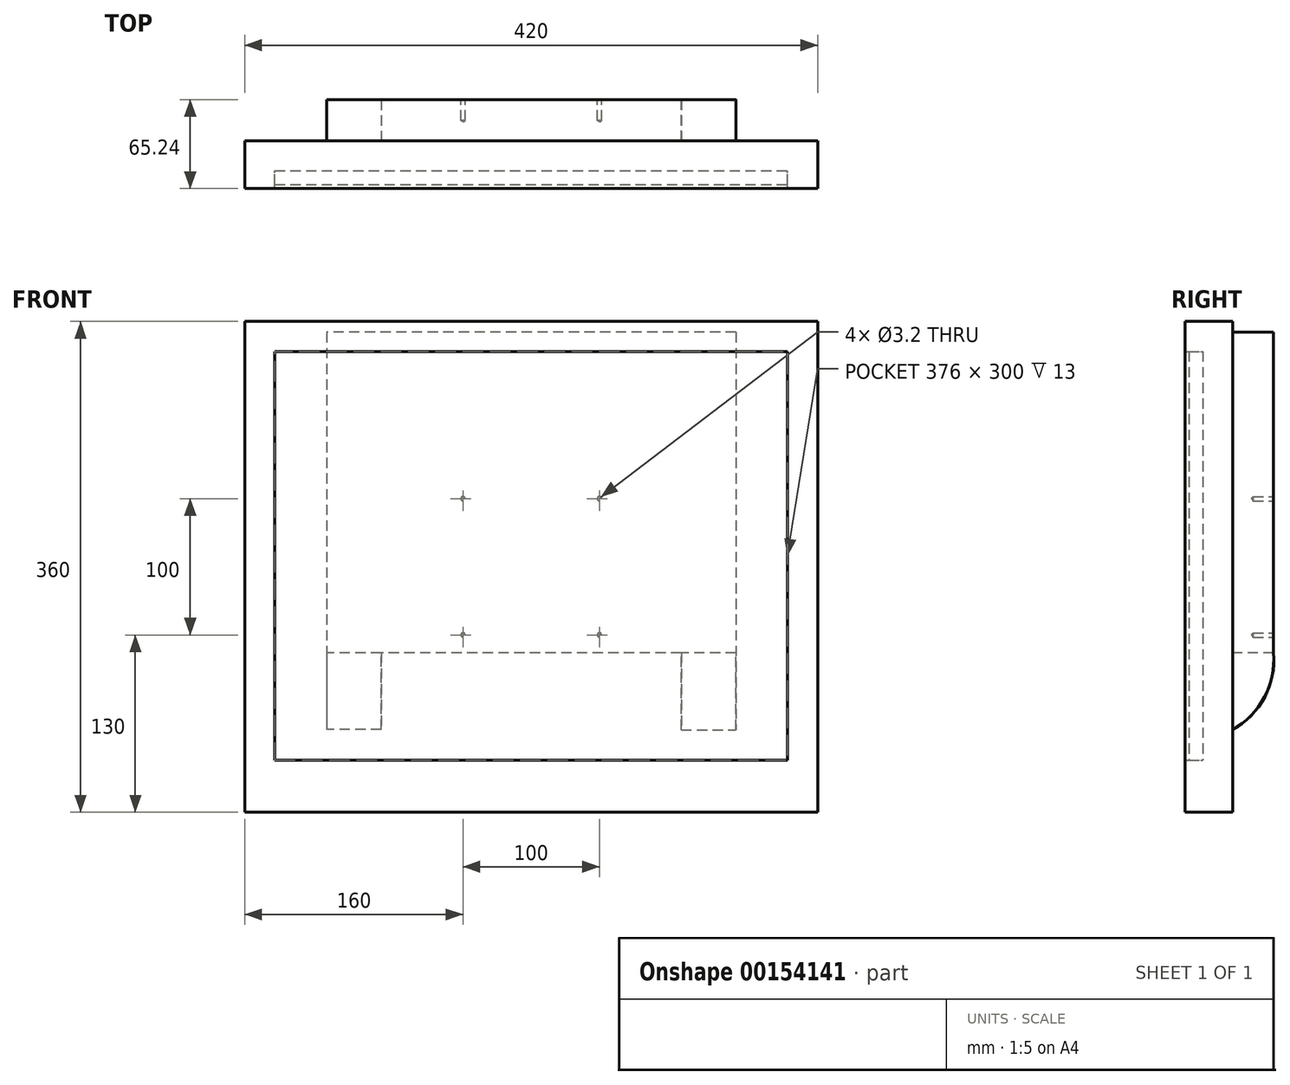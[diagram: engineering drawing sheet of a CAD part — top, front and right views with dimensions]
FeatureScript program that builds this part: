
annotation { "Feature Type Name" : "Feature", "Feature Type Description" : "" }
export const myFeature = defineFeature(function(context is Context, id is Id, definition is map)
    precondition{}
    {
        {
            var Q0;
            Q0=qCreatedBy(makeId("Front.planeOp"),FACE);
            var sketch = newSketch(context, id + "F0", { "sketchPlane" : qUnion([Q0])});
            skLineSegment(sketch, "E0.bottom", {"start": v(210, -180) * mm, "end": v(-210, -180) * mm});
            skLineSegment(sketch, "E0.top", {"start": v(210, 180) * mm, "end": v(-210, 180) * mm});
            skLineSegment(sketch, "E0.left", {"start": v(210, -180) * mm, "end": v(210, 180) * mm});
            skLineSegment(sketch, "E0.right", {"start": v(-210, -180) * mm, "end": v(-210, 180) * mm});
            skPoint(sketch, "E0.middle", {"position": v(0, 0) * mm});
            skLineSegment(sketch, "E1.bottom", {"start": v(-188, 158) * mm, "end": v(188, 158) * mm});
            skLineSegment(sketch, "E1.top", {"start": v(-188, -142) * mm, "end": v(188, -142) * mm});
            skLineSegment(sketch, "E1.left", {"start": v(-188, 158) * mm, "end": v(-188, -142) * mm});
            skLineSegment(sketch, "E1.right", {"start": v(188, 158) * mm, "end": v(188, -142) * mm});
            skSolve(sketch);
        }
        {
            var Q0;
            Q0 = qSketchRegion(id + "F0", true);
            extrude(context, id + "F1", {"entities" : qUnion([Q0]), "depth" : 13 * mm});
        }
        {
            var Q0;
            Q0=makeQuery(id+"F1.opExtrude","CAP_FACE",FACE,{"disambiguationData":[OSD([sQuery(id+"F0.wireOp",EDGE,"E0.bottom"),sQuery(id+"F0.wireOp",EDGE,"E0.top"),sQuery(id+"F0.wireOp",EDGE,"E0.left"),sQuery(id+"F0.wireOp",EDGE,"E0.right"),sQuery(id+"F0.wireOp",EDGE,"E1.bottom"),sQuery(id+"F0.wireOp",EDGE,"E1.top"),sQuery(id+"F0.wireOp",EDGE,"E1.left"),sQuery(id+"F0.wireOp",EDGE,"E1.right")])],"isStart":true});
            var sketch = newSketch(context, id + "F2", { "sketchPlane" : qUnion([Q0])});
            skLineSegment(sketch, "E2.bottom", {"start": v(-210, 180) * mm, "end": v(210, 180) * mm});
            skLineSegment(sketch, "E2.top", {"start": v(-210, -180) * mm, "end": v(210, -180) * mm});
            skLineSegment(sketch, "E2.left", {"start": v(-210, 180) * mm, "end": v(-210, -180) * mm});
            skLineSegment(sketch, "E2.right", {"start": v(210, 180) * mm, "end": v(210, -180) * mm});
            skSolve(sketch);
        }
        {
            var Q0;
            Q0 = qSketchRegion(id + "F2", true);
            extrude(context, id + "F3", {"entities" : qUnion([Q0]), "operationType" : NewBodyOperationType.ADD, "depth" : 22 * mm});
        }
        {
            var Q0;
            Q0=makeQuery(id+"F3.opExtrude","CAP_FACE",FACE,{"disambiguationData":[OSD([sQuery(id+"F2.wireOp",EDGE,"E2.bottom"),sQuery(id+"F2.wireOp",EDGE,"E2.top"),sQuery(id+"F2.wireOp",EDGE,"E2.left"),sQuery(id+"F2.wireOp",EDGE,"E2.right")])],"isStart":true});
            var sketch = newSketch(context, id + "F4", { "sketchPlane" : qUnion([Q0])});
            skLineSegment(sketch, "E3.bottom", {"start": v(-188, 158) * mm, "end": v(188, 158) * mm});
            skLineSegment(sketch, "E3.top", {"start": v(-188, -142) * mm, "end": v(188, -142) * mm});
            skLineSegment(sketch, "E3.left", {"start": v(-188, 158) * mm, "end": v(-188, -142) * mm});
            skLineSegment(sketch, "E3.right", {"start": v(188, 158) * mm, "end": v(188, -142) * mm});
            skSolve(sketch);
        }
        {
            var Q0;
            Q0 = qSketchRegion(id + "F4", true);
            extrude(context, id + "F5", {"entities" : qUnion([Q0]), "depth" : 10 * mm});
        }
        {
            var Q0;
            Q0=makeQuery(id+"F3.opExtrude","CAP_FACE",FACE,{"disambiguationData":[OSD([sQuery(id+"F2.wireOp",EDGE,"E2.bottom"),sQuery(id+"F2.wireOp",EDGE,"E2.top"),sQuery(id+"F2.wireOp",EDGE,"E2.left"),sQuery(id+"F2.wireOp",EDGE,"E2.right")])],"isStart":false});
            var sketch = newSketch(context, id + "F6", { "sketchPlane" : qUnion([Q0])});
            skLineSegment(sketch, "E4.bottom", {"start": v(-150, 172) * mm, "end": v(150, 172) * mm});
            skLineSegment(sketch, "E4.top", {"start": v(-150, -63) * mm, "end": v(150, -63) * mm});
            skLineSegment(sketch, "E4.left", {"start": v(-150, 172) * mm, "end": v(-150, -63) * mm});
            skLineSegment(sketch, "E4.right", {"start": v(150, 172) * mm, "end": v(150, -63) * mm});
            skSolve(sketch);
        }
        {
            var Q0;
            Q0 = qSketchRegion(id + "F6", true);
            extrude(context, id + "F7", {"entities" : qUnion([Q0]), "operationType" : NewBodyOperationType.ADD, "depth" : 30 * mm});
        }
        {
            var Q0;
            Q0=makeQuery(id+"F7.opExtrude","SWEPT_FACE",FACE,{"disambiguationData":[OSD([sQuery(id+"F6.wireOp",EDGE,"E4.left")])]});
            var sketch = newSketch(context, id + "F8", { "sketchPlane" : qUnion([Q0])});
            skArc(sketch, "E5", {"start": v(21.9, -119.54) * mm, "mid": v(45.19, -95.66) * mm, "end": v(52, -63) * mm});
            skLineSegment(sketch, "E6", {"start": v(52, -63) * mm, "end": v(22, -63) * mm});
            skLineSegment(sketch, "E7", {"start": v(22, -63) * mm, "end": v(21.9, -119.54) * mm});
            skSolve(sketch);
        }
        {
            var Q0;
            Q0 = qSketchRegion(id + "F8", true);
            extrude(context, id + "F9", {"entities" : qUnion([Q0]), "operationType" : NewBodyOperationType.ADD, "oppositeDirection" : true, "depth" : 40 * mm});
        }
        {
            var Q0;
            Q0=makeQuery(id+"F7.opExtrude","SWEPT_FACE",FACE,{"disambiguationData":[OSD([sQuery(id+"F6.wireOp",EDGE,"E4.right")])]});
            var sketch = newSketch(context, id + "F10", { "sketchPlane" : qUnion([Q0])});
            skArc(sketch, "E8", {"start": v(-52, -63) * mm, "mid": v(-45.4, -95.72) * mm, "end": v(-21.9, -119.45) * mm});
            skLineSegment(sketch, "E9", {"start": v(-52, -63) * mm, "end": v(-22, -63) * mm});
            skLineSegment(sketch, "E10", {"start": v(-22, -63) * mm, "end": v(-21.9, -119.45) * mm});
            skSolve(sketch);
        }
        {
            var Q0;
            Q0 = qSketchRegion(id + "F10", true);
            extrude(context, id + "F11", {"entities" : qUnion([Q0]), "operationType" : NewBodyOperationType.ADD, "oppositeDirection" : true, "depth" : 40 * mm});
        }
        {
            var Q0;
            Q0=makeQuery(id+"F7.opExtrude","CAP_FACE",FACE,{"disambiguationData":[OSD([sQuery(id+"F6.wireOp",EDGE,"E4.bottom"),sQuery(id+"F6.wireOp",EDGE,"E4.top"),sQuery(id+"F6.wireOp",EDGE,"E4.left"),sQuery(id+"F6.wireOp",EDGE,"E4.right")])],"isStart":false});
            var sketch = newSketch(context, id + "F12", { "sketchPlane" : qUnion([Q0])});
            skPoint(sketch, "E11", {"position": v(50, -50) * mm});
            skPoint(sketch, "E12", {"position": v(50, 50) * mm});
            skPoint(sketch, "E13", {"position": v(-50, 50) * mm});
            skPoint(sketch, "E14", {"position": v(-50, -50) * mm});
            skLineSegment(sketch, "E15", {"start": v(-50, 50) * mm, "end": v(50, 50) * mm});
            skLineSegment(sketch, "E16", {"start": v(50, 50) * mm, "end": v(50, -50) * mm});
            skLineSegment(sketch, "E17", {"start": v(50, -50) * mm, "end": v(-50, -50) * mm});
            skLineSegment(sketch, "E18", {"start": v(-50, -50) * mm, "end": v(-50, 50) * mm});
            skSolve(sketch);
        }
        {
            var Q0;
            Q0=sQuery(id+"F12.wireOp",VERTEX,"E13");
            var Q1;
            Q1=sQuery(id+"F12.wireOp",VERTEX,"E12");
            var Q2;
            Q2=sQuery(id+"F12.wireOp",VERTEX,"E11");
            var Q3;
            Q3=sQuery(id+"F12.wireOp",VERTEX,"E14");
            var Q4;
            Q4=makeQuery(id+"F1.opExtrude","SWEPT_BODY",BODY,{"disambiguationData":[OSD([sQuery(id+"F0.wireOp",EDGE,"E0.bottom"),sQuery(id+"F0.wireOp",EDGE,"E0.top"),sQuery(id+"F0.wireOp",EDGE,"E0.left"),sQuery(id+"F0.wireOp",EDGE,"E0.right"),sQuery(id+"F0.wireOp",EDGE,"E1.bottom"),sQuery(id+"F0.wireOp",EDGE,"E1.top"),sQuery(id+"F0.wireOp",EDGE,"E1.left"),sQuery(id+"F0.wireOp",EDGE,"E1.right")])]});
            hole(context, id + "F13", {"style" : HoleStyle.SIMPLE, "endStyle" : HoleEndStyle.BLIND, "standardTappedOrClearance" : lookupTablePath({ "standard" : "ISO", "engagement" : "75%", "pitch" : "0.75 mm", "size" : "M4", "type" : "Tapped" }), "standardBlindInLast" : lookupTablePath({ "standard" : "ISO", "engagement" : "75%", "pitch" : "0.75 mm", "size" : "M4", "type" : "Tapped" }), "holeDiameter" : 3.2 * mm, "holeDepth" : 15 * mm, "locations" : qUnion([Q0, Q1, Q2, Q3]), "scope" : qUnion([Q4])});
        }
    });
